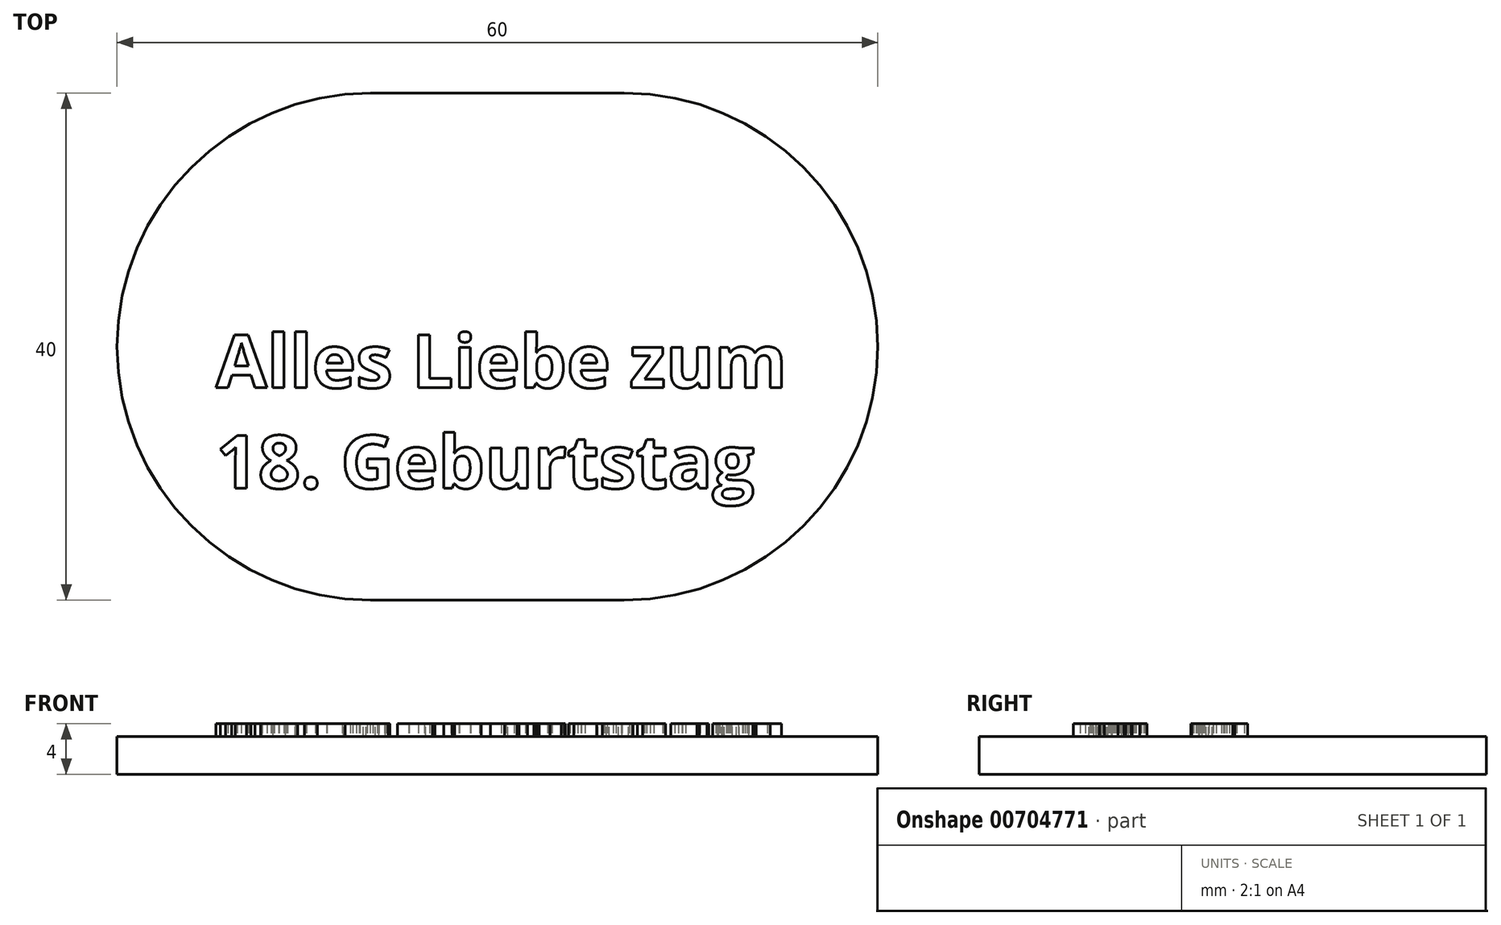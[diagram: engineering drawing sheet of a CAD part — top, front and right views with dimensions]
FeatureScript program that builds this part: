
annotation { "Feature Type Name" : "Feature", "Feature Type Description" : "" }
export const myFeature = defineFeature(function(context is Context, id is Id, definition is map)
    precondition{}
    {
        {
            var Q0;
            Q0=qCreatedBy(makeId("Top.planeOp"),FACE);
            var sketch = newSketch(context, id + "F0", { "sketchPlane" : qUnion([Q0])});
            skLineSegment(sketch, "E0.bottom", {"start": v(10, -20) * mm, "end": v(-10, -20) * mm});
            skLineSegment(sketch, "E0.top", {"start": v(10, 20) * mm, "end": v(-10, 20) * mm});
            skLineSegment(sketch, "E0.left", {"start": v(10, -20) * mm, "end": v(10, 20) * mm});
            skLineSegment(sketch, "E0.right", {"start": v(-10, -20) * mm, "end": v(-10, 20) * mm});
            skPoint(sketch, "E0.middle", {"position": v(0, 0) * mm});
            skArc(sketch, "E1", {"start": v(-10, 20) * mm, "mid": v(-30, 0) * mm, "end": v(-10, -20) * mm});
            skArc(sketch, "E2", {"start": v(10, -20) * mm, "mid": v(30, 0) * mm, "end": v(10, 20) * mm});
            skSolve(sketch);
        }
        {
            var Q0;
            Q0=makeQuery(id+"F0.imprint","IMPRINT",FACE,{"disambiguationData":[TD([[makeQuery(id+"F0.imprint","IMPRINT",EDGE,{"derivedFrom":sQuery(id+"F0.wireOp",EDGE,"E0.right")}),1.0]])]});
            var Q1;
            Q1=makeQuery(id+"F0.imprint","IMPRINT",FACE,{"disambiguationData":[TD([[makeQuery(id+"F0.imprint","IMPRINT",EDGE,{"derivedFrom":sQuery(id+"F0.wireOp",EDGE,"E0.bottom")}),-1.0]])]});
            var Q2;
            Q2=makeQuery(id+"F0.imprint","IMPRINT",FACE,{"disambiguationData":[TD([[makeQuery(id+"F0.imprint","IMPRINT",EDGE,{"derivedFrom":sQuery(id+"F0.wireOp",EDGE,"E0.left")}),-1.0]])]});
            extrude(context, id + "F1", {"entities" : qUnion([Q0, Q1, Q2]), "depth" : 3 * mm, "offsetDistance" : 25 * mm});
        }
        {
            var Q0;
            Q0=makeQuery(id+"F1.opExtrude","CAP_FACE",FACE,{"disambiguationData":[OSD([sQuery(id+"F0.wireOp",EDGE,"E0.bottom"),sQuery(id+"F0.wireOp",EDGE,"E0.top"),sQuery(id+"F0.wireOp",EDGE,"E1"),sQuery(id+"F0.wireOp",EDGE,"E2")])],"isStart":false});
            var sketch = newSketch(context, id + "F2", { "sketchPlane" : qUnion([Q0])});
            skText(sketch, "E3", { "text": "Alles Liebe zum\n18. Geburtstag", "fontName": "OpenSans-Bold.ttf"});
            const initialGuessF2  = {"E3": [-0.0222, -0.00325, 1, 0, 0.0042]};
            skSetInitialGuess(sketch, initialGuessF2);
            skSolve(sketch);
        }
        {
            var Q0;
            Q0 = qSketchRegion(id + "F2", true);
            extrude(context, id + "F3", {"entities" : qUnion([Q0]), "operationType" : NewBodyOperationType.ADD, "depth" : 1 * mm, "offsetDistance" : 25 * mm});
        }
    });
